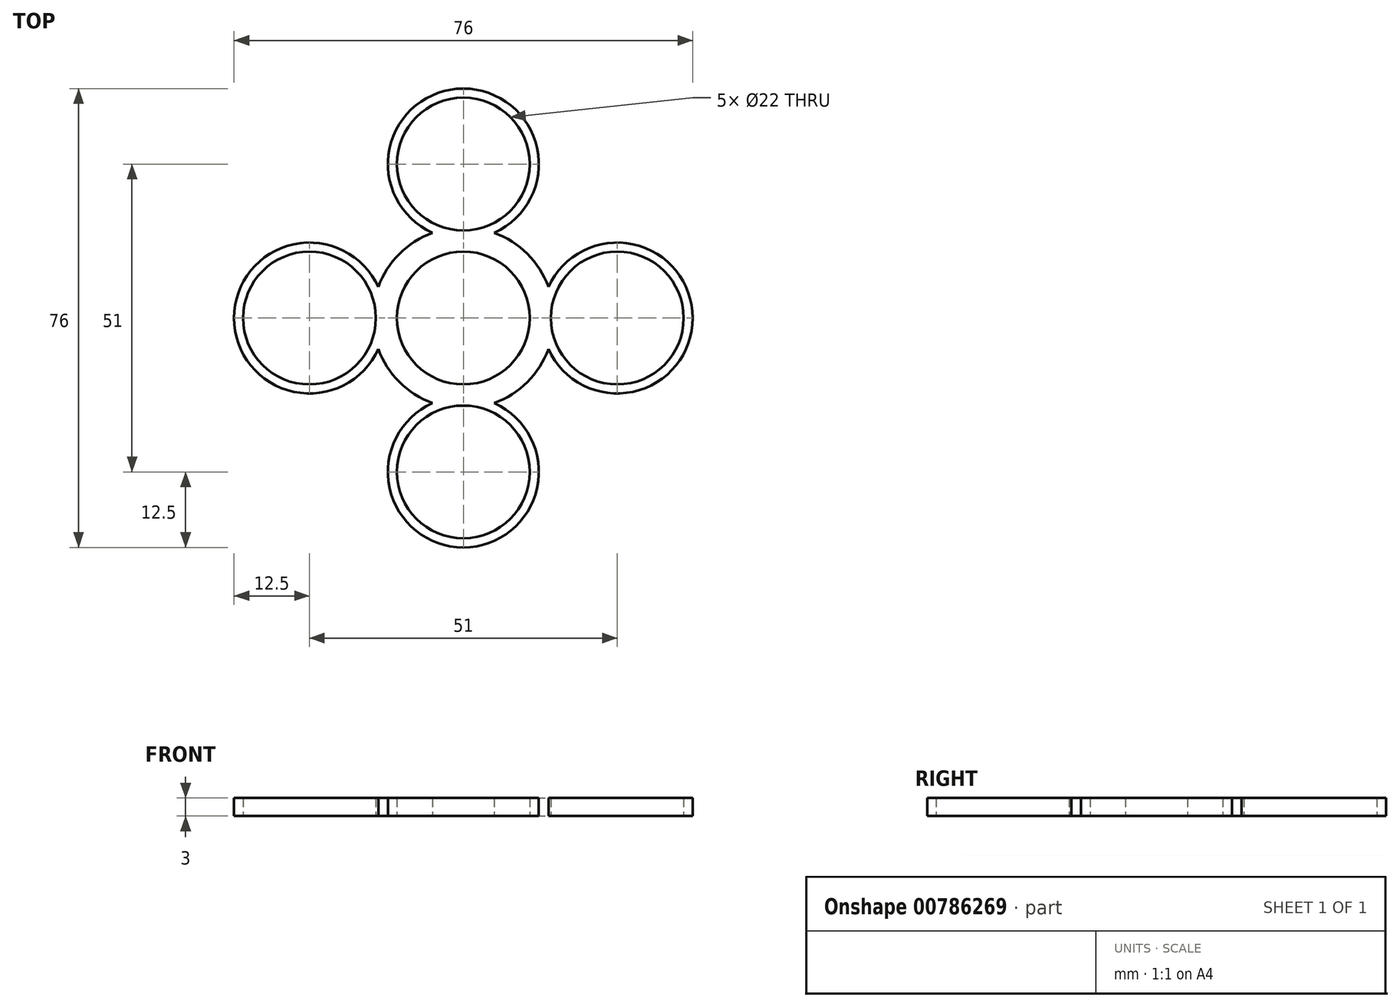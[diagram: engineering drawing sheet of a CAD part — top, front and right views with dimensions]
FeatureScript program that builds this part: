
annotation { "Feature Type Name" : "Feature", "Feature Type Description" : "" }
export const myFeature = defineFeature(function(context is Context, id is Id, definition is map)
    precondition{}
    {
        {
            var Q0;
            Q0=qCreatedBy(makeId("Top.planeOp"),FACE);
            var sketch = newSketch(context, id + "F0", { "sketchPlane" : qUnion([Q0])});
            skArc(sketch, "E0", {"start": v(7.78, 7.78) * mm, "mid": v(0, 11) * mm, "end": v(-7.78, 7.78) * mm});
            skArc(sketch, "E1", {"start": v(-5.12, 14.1) * mm, "mid": v(-8.06, 12.65) * mm, "end": v(-10.6, 10.6) * mm});
            skCircle(sketch, "E2", {"center": v(0, 25.5) * mm, "radius": 11 * mm});
            skArc(sketch, "E3", {"start": v(5.12, 14.1) * mm, "mid": v(0, 38) * mm, "end": v(-5.12, 14.1) * mm});
            skArc(sketch, "E4.trimOffspring", {"start": v(10.6, 10.6) * mm, "mid": v(8.06, 12.65) * mm, "end": v(5.12, 14.1) * mm});
            skCircle(sketch, "E5.1.0", {"center": v(-25.5, 0) * mm, "radius": 11 * mm});
            skArc(sketch, "E5.1.1", {"start": v(-14.1, 5.12) * mm, "mid": v(-38, 0) * mm, "end": v(-14.1, -5.12) * mm});
            skArc(sketch, "E5.1.2", {"start": v(-10.6, 10.6) * mm, "mid": v(-12.65, 8.06) * mm, "end": v(-14.1, 5.12) * mm});
            skArc(sketch, "E5.1.3", {"start": v(-14.1, -5.12) * mm, "mid": v(-12.65, -8.06) * mm, "end": v(-10.6, -10.6) * mm});
            skArc(sketch, "E5.1.4", {"start": v(-7.78, 7.78) * mm, "mid": v(-11, 0) * mm, "end": v(-7.78, -7.78) * mm});
            skCircle(sketch, "E5.2.0", {"center": v(0, -25.5) * mm, "radius": 11 * mm});
            skArc(sketch, "E5.2.1", {"start": v(-5.12, -14.1) * mm, "mid": v(0, -38) * mm, "end": v(5.12, -14.1) * mm});
            skArc(sketch, "E5.2.2", {"start": v(-10.6, -10.6) * mm, "mid": v(-8.06, -12.65) * mm, "end": v(-5.12, -14.1) * mm});
            skArc(sketch, "E5.2.3", {"start": v(5.12, -14.1) * mm, "mid": v(8.06, -12.65) * mm, "end": v(10.6, -10.6) * mm});
            skArc(sketch, "E5.2.4", {"start": v(-7.78, -7.78) * mm, "mid": v(0, -11) * mm, "end": v(7.78, -7.78) * mm});
            skCircle(sketch, "E5.3.0", {"center": v(25.5, 0) * mm, "radius": 11 * mm});
            skArc(sketch, "E5.3.1", {"start": v(14.1, -5.12) * mm, "mid": v(38, 0) * mm, "end": v(14.1, 5.12) * mm});
            skArc(sketch, "E5.3.2", {"start": v(10.6, -10.6) * mm, "mid": v(12.65, -8.06) * mm, "end": v(14.1, -5.12) * mm});
            skArc(sketch, "E5.3.3", {"start": v(14.1, 5.12) * mm, "mid": v(12.65, 8.06) * mm, "end": v(10.6, 10.6) * mm});
            skArc(sketch, "E5.3.4", {"start": v(7.78, -7.78) * mm, "mid": v(11, 0) * mm, "end": v(7.78, 7.78) * mm});
            skSolve(sketch);
        }
        {
            var Q0;
            Q0 = qSketchRegion(id + "F0", true);
            extrude(context, id + "F1", {"entities" : qUnion([Q0]), "depth" : 3 * mm, "offsetDistance" : 25 * mm});
        }
    });
